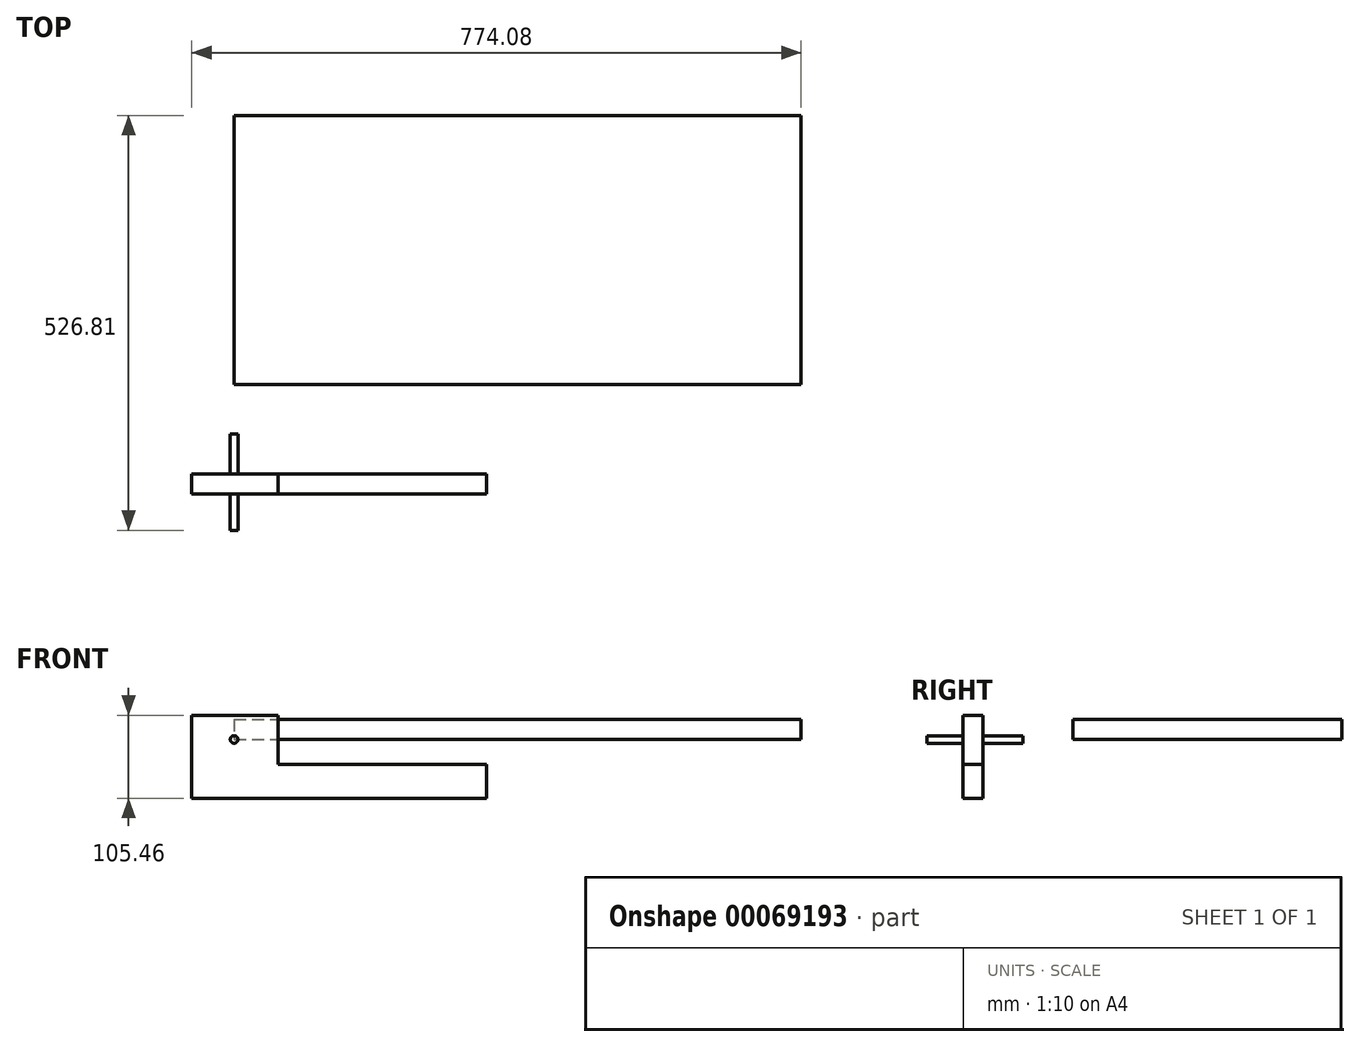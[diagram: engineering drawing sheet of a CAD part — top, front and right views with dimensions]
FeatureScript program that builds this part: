
annotation { "Feature Type Name" : "Feature", "Feature Type Description" : "" }
export const myFeature = defineFeature(function(context is Context, id is Id, definition is map)
    precondition{}
    {
        {
            var Q0;
            Q0=qCreatedBy(makeId("Front.planeOp"),FACE);
            var sketch = newSketch(context, id + "F0", { "sketchPlane" : qUnion([Q0])});
            skLineSegment(sketch, "E0.bottom", {"start": v(-53.88, 30.7) * mm, "end": v(55.84, 30.7) * mm});
            skLineSegment(sketch, "E0.top", {"start": v(-53.88, -45.72) * mm, "end": v(55.84, -45.72) * mm});
            skLineSegment(sketch, "E0.left", {"start": v(-53.88, 30.7) * mm, "end": v(-53.88, -45.72) * mm});
            skLineSegment(sketch, "E0.right", {"start": v(55.84, 30.7) * mm, "end": v(55.84, -45.72) * mm});
            skSolve(sketch);
        }
        {
            var Q0;
            Q0 = qSketchRegion(id + "F0", true);
            extrude(context, id + "F1", {"entities" : qUnion([Q0]), "depth" : 25.4 * mm});
        }
        {
            var Q0;
            Q0=makeQuery(id+"F1.opExtrude","CAP_FACE",FACE,{"disambiguationData":[OSD([sQuery(id+"F0.wireOp",EDGE,"E0.bottom"),sQuery(id+"F0.wireOp",EDGE,"E0.top"),sQuery(id+"F0.wireOp",EDGE,"E0.left"),sQuery(id+"F0.wireOp",EDGE,"E0.right")])],"isStart":false});
            var sketch = newSketch(context, id + "F2", { "sketchPlane" : qUnion([Q0])});
            skCircle(sketch, "E1", {"center": v(0, 0) * mm, "radius": 4.8 * mm});
            skSolve(sketch);
        }
        {
            var Q0;
            Q0=makeQuery(id+"F2.imprint","IMPRINT",FACE,{"disambiguationData":[TD([[makeQuery(id+"F2.imprint","IMPRINT",EDGE,{"derivedFrom":sQuery(id+"F2.wireOp",EDGE,"E1")}),1.0]])]});
            extrude(context, id + "F3", {"entities" : qUnion([Q0]), "operationType" : NewBodyOperationType.ADD, "depth" : 45.87 * mm, "hasSecondDirection" : true, "secondDirectionOppositeDirection" : true, "secondDirectionDepth" : 76.2 * mm});
        }
        {
            var Q0;
            Q0=makeQuery(id+"F1.opExtrude","CAP_FACE",FACE,{"disambiguationData":[OSD([sQuery(id+"F0.wireOp",EDGE,"E0.bottom"),sQuery(id+"F0.wireOp",EDGE,"E0.top"),sQuery(id+"F0.wireOp",EDGE,"E0.left"),sQuery(id+"F0.wireOp",EDGE,"E0.right")])],"isStart":false});
            var sketch = newSketch(context, id + "F4", { "sketchPlane" : qUnion([Q0])});
            skLineSegment(sketch, "E2.bottom", {"start": v(-53.88, -31.94) * mm, "end": v(321.01, -31.94) * mm});
            skLineSegment(sketch, "E2.top", {"start": v(-53.88, -74.76) * mm, "end": v(321.01, -74.76) * mm});
            skLineSegment(sketch, "E2.left", {"start": v(-53.88, -31.94) * mm, "end": v(-53.88, -74.76) * mm});
            skLineSegment(sketch, "E2.right", {"start": v(321.01, -31.94) * mm, "end": v(321.01, -74.76) * mm});
            skSolve(sketch);
        }
        {
            var Q0;
            Q0 = qSketchRegion(id + "F4", true);
            extrude(context, id + "F5", {"entities" : qUnion([Q0]), "operationType" : NewBodyOperationType.ADD, "oppositeDirection" : true, "depth" : 25.4 * mm});
        }
        {
            var Q0;
            Q0=qCreatedBy(makeId("Top.planeOp"),FACE);
            var sketch = newSketch(context, id + "F6", { "sketchPlane" : qUnion([Q0])});
            skLineSegment(sketch, "E3.bottom", {"start": v(0, 455.54) * mm, "end": v(720.2, 455.54) * mm});
            skLineSegment(sketch, "E3.top", {"start": v(0, 114.18) * mm, "end": v(720.2, 114.18) * mm});
            skLineSegment(sketch, "E3.left", {"start": v(0, 455.54) * mm, "end": v(0, 114.18) * mm});
            skLineSegment(sketch, "E3.right", {"start": v(720.2, 455.54) * mm, "end": v(720.2, 114.18) * mm});
            skSolve(sketch);
        }
        {
            var Q0;
            Q0 = qSketchRegion(id + "F6", true);
            extrude(context, id + "F7", {"entities" : qUnion([Q0]), "depth" : 25.4 * mm});
        }
    });
